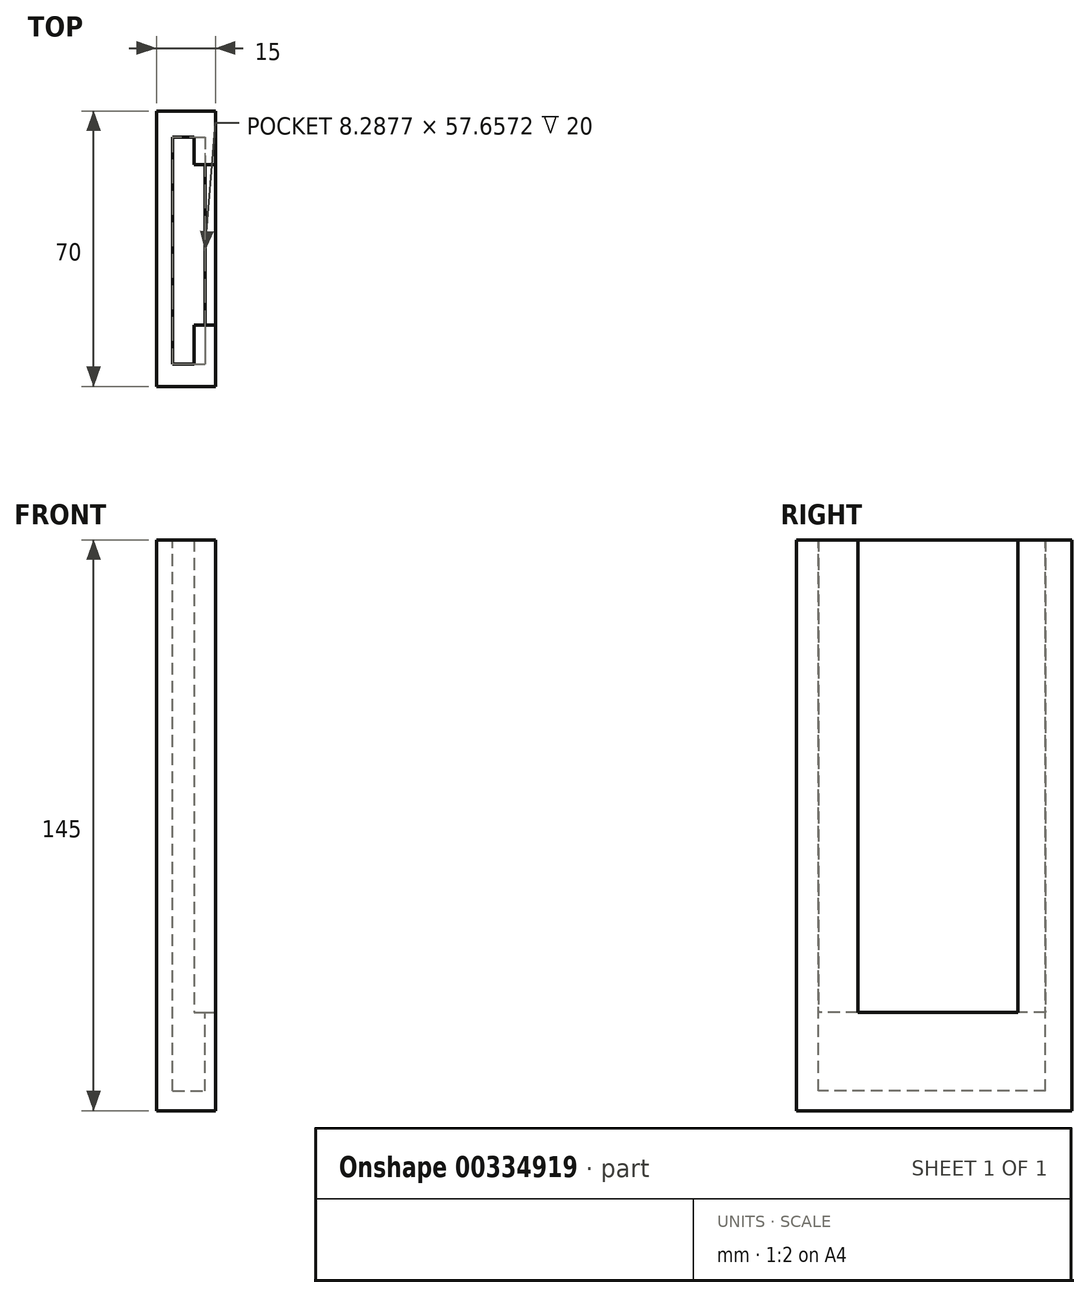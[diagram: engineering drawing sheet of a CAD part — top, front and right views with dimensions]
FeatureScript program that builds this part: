
annotation { "Feature Type Name" : "Feature", "Feature Type Description" : "" }
export const myFeature = defineFeature(function(context is Context, id is Id, definition is map)
    precondition{}
    {
        {
            var Q0;
            Q0=qCreatedBy(makeId("Top.planeOp"),FACE);
            var sketch = newSketch(context, id + "F0", { "sketchPlane" : qUnion([Q0])});
            skLineSegment(sketch, "E0.bottom", {"start": v(-10.06, 69.84) * mm, "end": v(-0.06, 69.84) * mm});
            skLineSegment(sketch, "E0.top", {"start": v(-10.06, -0.16) * mm, "end": v(-0.06, -0.16) * mm});
            skLineSegment(sketch, "E0.left", {"start": v(-10.06, 69.84) * mm, "end": v(-10.06, -0.16) * mm});
            skLineSegment(sketch, "E0.right", {"start": v(-0.06, 69.84) * mm, "end": v(-0.06, -0.16) * mm});
            skSolve(sketch);
        }
        {
            var Q0;
            Q0=makeQuery(id+"F0.imprint","IMPRINT",FACE,{"disambiguationData":[TD([[makeQuery(id+"F0.imprint","IMPRINT",EDGE,{"derivedFrom":sQuery(id+"F0.wireOp",EDGE,"E0.bottom")}),-1.0]])]});
            extrude(context, id + "F1", {"entities" : qUnion([Q0]), "depth" : 145 * mm});
        }
        {
            var Q0;
            Q0=makeQuery(id+"F1.opExtrude","SWEPT_FACE",FACE,{"disambiguationData":[OSD([sQuery(id+"F0.wireOp",EDGE,"E0.right")])]});
            extrude(context, id + "F2", {"entities" : qUnion([Q0]), "operationType" : NewBodyOperationType.ADD, "depth" : 5 * mm});
        }
        {
            var Q0;
            {var subQ0=sQuery(id+"F0.wireOp",EDGE,"E0.right");Q0=makeQuery(id+"F2.boolean.opBoolean","MERGE",FACE,{"derivedFrom":[makeQuery(id+"F1.opExtrude","CAP_FACE",FACE,{"disambiguationData":[OSD([sQuery(id+"F0.wireOp",EDGE,"E0.bottom"),sQuery(id+"F0.wireOp",EDGE,"E0.top"),sQuery(id+"F0.wireOp",EDGE,"E0.left"),subQ0])],"isStart":false}),makeQuery(id+"F2.opExtrude","SWEPT_FACE",FACE,{"disambiguationData":[OSD([subQ0]),TDD([makeQuery(id+"F1.opExtrude","CAP_EDGE",EDGE,{"disambiguationData":[OSD([subQ0])],"isStart":false})])]})]});}
            var sketch = newSketch(context, id + "F3", { "sketchPlane" : qUnion([Q0])});
            skLineSegment(sketch, "E1.bottom", {"start": v(-5.95, 63.14) * mm, "end": v(2.33, 63.14) * mm});
            skLineSegment(sketch, "E1.top", {"start": v(-5.95, 5.48) * mm, "end": v(2.33, 5.48) * mm});
            skLineSegment(sketch, "E1.left", {"start": v(-5.95, 63.14) * mm, "end": v(-5.95, 5.48) * mm});
            skLineSegment(sketch, "E1.right", {"start": v(2.33, 63.14) * mm, "end": v(2.33, 5.48) * mm});
            skSolve(sketch);
        }
        {
            var Q0;
            Q0=makeQuery(id+"F3.imprint","IMPRINT",FACE,{"disambiguationData":[TD([[makeQuery(id+"F3.imprint","IMPRINT",EDGE,{"derivedFrom":sQuery(id+"F3.wireOp",EDGE,"E1.bottom")}),-1.0]])]});
            extrude(context, id + "F4", {"entities" : qUnion([Q0]), "operationType" : NewBodyOperationType.REMOVE, "oppositeDirection" : true, "depth" : 140 * mm});
        }
        {
            var Q0;
            {var subQ0=sQuery(id+"F0.wireOp",EDGE,"E0.right");Q0=makeQuery(id+"F2.boolean.opBoolean","MERGE",FACE,{"derivedFrom":[makeQuery(id+"F1.opExtrude","CAP_FACE",FACE,{"disambiguationData":[OSD([sQuery(id+"F0.wireOp",EDGE,"E0.bottom"),sQuery(id+"F0.wireOp",EDGE,"E0.top"),sQuery(id+"F0.wireOp",EDGE,"E0.left"),subQ0])],"isStart":false}),makeQuery(id+"F2.opExtrude","SWEPT_FACE",FACE,{"disambiguationData":[OSD([subQ0]),TDD([makeQuery(id+"F1.opExtrude","CAP_EDGE",EDGE,{"disambiguationData":[OSD([subQ0])],"isStart":false})])]})]});}
            var sketch = newSketch(context, id + "F5", { "sketchPlane" : qUnion([Q0])});
            skLineSegment(sketch, "E2", {"start": v(2.33, 63.14) * mm, "end": v(4.94, 63.14) * mm});
            skLineSegment(sketch, "E3", {"start": v(2.33, 5.48) * mm, "end": v(4.94, 5.48) * mm});
            skSolve(sketch);
        }
        {
            var Q0;
            {var subQ0=sQuery(id+"F5.wireOp",EDGE,"E2");Q0=makeQuery(id+"F5.imprint","IMPRINT",FACE,{"disambiguationData":[TD([[makeQuery(id+"F5.imprint","IMPRINT",EDGE,{"derivedFrom":subQ0}),-1.0]])]});}
            extrude(context, id + "F6", {"entities" : qUnion([Q0]), "operationType" : NewBodyOperationType.REMOVE, "oppositeDirection" : true, "depth" : 120 * mm});
        }
        {
            var Q0;
            Q0=makeQuery(id+"F6.boolean.opBoolean","MERGE",FACE,{"derivedFrom":[makeQuery(id+"F4.boolean.opBoolean","COPY",FACE,{"derivedFrom":makeQuery(id+"F4.opExtrude","SWEPT_FACE",FACE,{"disambiguationData":[OSD([sQuery(id+"F3.wireOp",EDGE,"E1.top")])]})}),makeQuery(id+"F6.opExtrude","SWEPT_FACE",FACE,{"disambiguationData":[OSD([sQuery(id+"F5.wireOp",EDGE,"E3")])]})]});
            var sketch = newSketch(context, id + "F7", { "sketchPlane" : qUnion([Q0])});
            skLineSegment(sketch, "E4", {"start": v(0.5, 145) * mm, "end": v(0.5, 25) * mm});
            skLineSegment(sketch, "E5", {"start": v(0.5, 25) * mm, "end": v(5.95, 25) * mm});
            skLineSegment(sketch, "E6", {"start": v(5.95, 25) * mm, "end": v(-4.94, 25) * mm});
            skSolve(sketch);
        }
        {
            var Q0;
            {var subQ3=sQuery(id+"F7.wireOp",EDGE,"E4");Q0=makeQuery(id+"F7.imprint","IMPRINT",FACE,{"disambiguationData":[TD([[makeQuery(id+"F7.imprint","IMPRINT",EDGE,{"derivedFrom":subQ3}),-1.0]])]});}
            extrude(context, id + "F8", {"entities" : qUnion([Q0]), "operationType" : NewBodyOperationType.ADD, "depth" : 10 * mm});
        }
        {
            var Q0;
            Q0=makeQuery(id+"F6.boolean.opBoolean","MERGE",FACE,{"derivedFrom":[makeQuery(id+"F4.boolean.opBoolean","COPY",FACE,{"derivedFrom":makeQuery(id+"F4.opExtrude","SWEPT_FACE",FACE,{"disambiguationData":[OSD([sQuery(id+"F3.wireOp",EDGE,"E1.bottom")])]})}),makeQuery(id+"F6.opExtrude","SWEPT_FACE",FACE,{"disambiguationData":[OSD([sQuery(id+"F5.wireOp",EDGE,"E2")])]})]});
            var sketch = newSketch(context, id + "F9", { "sketchPlane" : qUnion([Q0])});
            skLineSegment(sketch, "E7", {"start": v(-0.5, 145) * mm, "end": v(-0.5, 25) * mm});
            skLineSegment(sketch, "E8", {"start": v(-0.5, 25) * mm, "end": v(4.94, 25) * mm});
            skLineSegment(sketch, "E9", {"start": v(-0.5, 25) * mm, "end": v(-5.95, 25) * mm});
            skSolve(sketch);
        }
        {
            var Q0;
            {var subQ5=sQuery(id+"F9.wireOp",EDGE,"E7");Q0=makeQuery(id+"F9.imprint","IMPRINT",FACE,{"disambiguationData":[TD([[makeQuery(id+"F9.imprint","IMPRINT",EDGE,{"derivedFrom":subQ5}),1.0]])]});}
            extrude(context, id + "F10", {"entities" : qUnion([Q0]), "operationType" : NewBodyOperationType.ADD, "depth" : 7 * mm});
        }
    });
